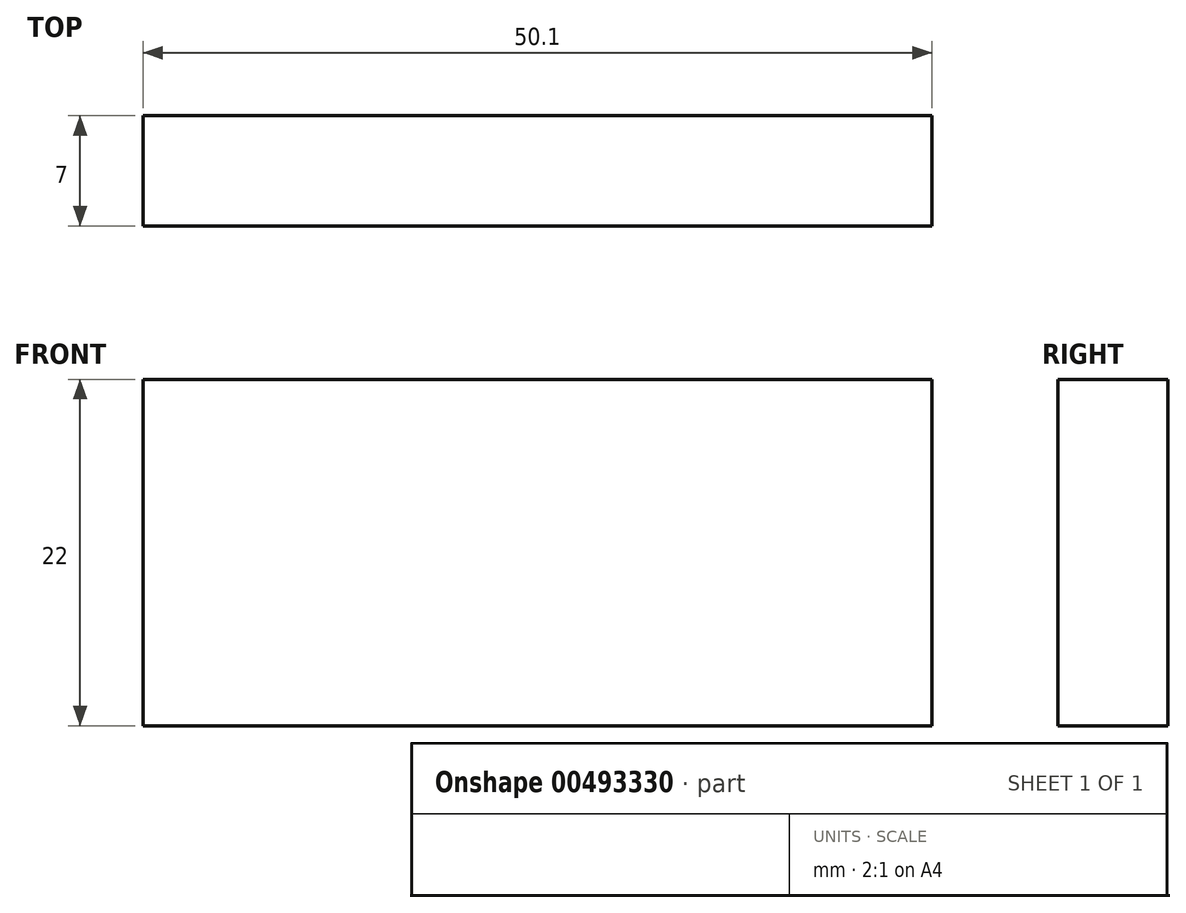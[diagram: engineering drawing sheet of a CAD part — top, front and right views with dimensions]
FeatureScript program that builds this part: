
annotation { "Feature Type Name" : "Feature", "Feature Type Description" : "" }
export const myFeature = defineFeature(function(context is Context, id is Id, definition is map)
    precondition{}
    {
        {
            var Q0;
            Q0=qCreatedBy(makeId("Front.planeOp"),FACE);
            var sketch = newSketch(context, id + "F0", { "sketchPlane" : qUnion([Q0])});
            skLineSegment(sketch, "E0.bottom", {"start": v(25.05, 11) * mm, "end": v(-25.05, 11) * mm});
            skLineSegment(sketch, "E0.top", {"start": v(25.05, -11) * mm, "end": v(-25.05, -11) * mm});
            skLineSegment(sketch, "E0.left", {"start": v(25.05, 11) * mm, "end": v(25.05, -11) * mm});
            skLineSegment(sketch, "E0.right", {"start": v(-25.05, 11) * mm, "end": v(-25.05, -11) * mm});
            skPoint(sketch, "E0.middle", {"position": v(0, 0) * mm});
            skSolve(sketch);
        }
        {
            var Q0;
            Q0 = qSketchRegion(id + "F0", true);
            extrude(context, id + "F1", {"entities" : qUnion([Q0]), "endBound" : BoundingType.SYMMETRIC, "depth" : 7 * mm});
        }
    });
